# Revit family: Operable-Wall
name_source: partatom
category: Generic Models
units: mm (PartAtom-declared; Revit-internal decimal feet)

## family parameters
Always vertical = Yes
Can host rebar = No
Classification Number = 23.25.40.17
Cut with Voids When Loaded = No
Maintain Annotation Orientation = No
Part Type = Normal
Room Calculation Point = No
Round Connector Dimension = Use Diameter
Shared = No
Work Plane-Based = No

## types (1)
- ByType
    Assembly Code = F1030900
    Carrier System = Multi-Directional Aluminum Track capable of supporting up to 425 lb. live load per panel

Multi-Directional Aluminum Track: certified to be capable of supporting up to 425 lb. (193 kg) of total live load weight per panel.

Multi-Directional Aluminum Track: certified to be capable of supporting up to 425 lb. (193 kg) of total live load weight per panel.

Multi-Directional Aluminum Track: certified to be capable of supporting up to 425 lb. (193 kg) of total live load weight per panel.
    Construction Details = http://www.arcat.com
    Default Elevation = 0' - 0"
    Depth = 0' - 1"
    Description = Operable Partition Wall
    End Panel = ARCAT - Textiles - Marquesa Lana - Green
    Expected Lifespan (Years) = 20
    First Panel = 6' - 3"
    Green Building-LEED = http://www.arcat.com
    Height = 16' - 0"
    Keynote = 10250
    Length = 50' - 0"
    Maintenance Schedule (Months) = 6
    Manufacturer = Generic
    Manufacturer Fax = (203) 939-2444
    Manufacturer Website = http://www.arcat.com
    Model = Generic
    Panel = 12' - 6"
    Panel Weight - Lb/SqFt = 6.5
    Product Data = http://www.arcat.com
    Product Properties = http://www.arcat.com
    STC Rating = 39
    Specification = http://www.arcat.com
    Upper Track Material = ARCAT - Metal - Steel - BHMA639 - Dull Bronze
    Vertical Trim Seals = Flexible Vinyl
    Wall Finish = ARCAT - Textiles - Marquesa Lana - Green
    Warranty Duration (Years) = 5

## geometry (parser evidence)
native form markers: Blend x3, Sweep x5
no freeform markers — native parametric forms only
